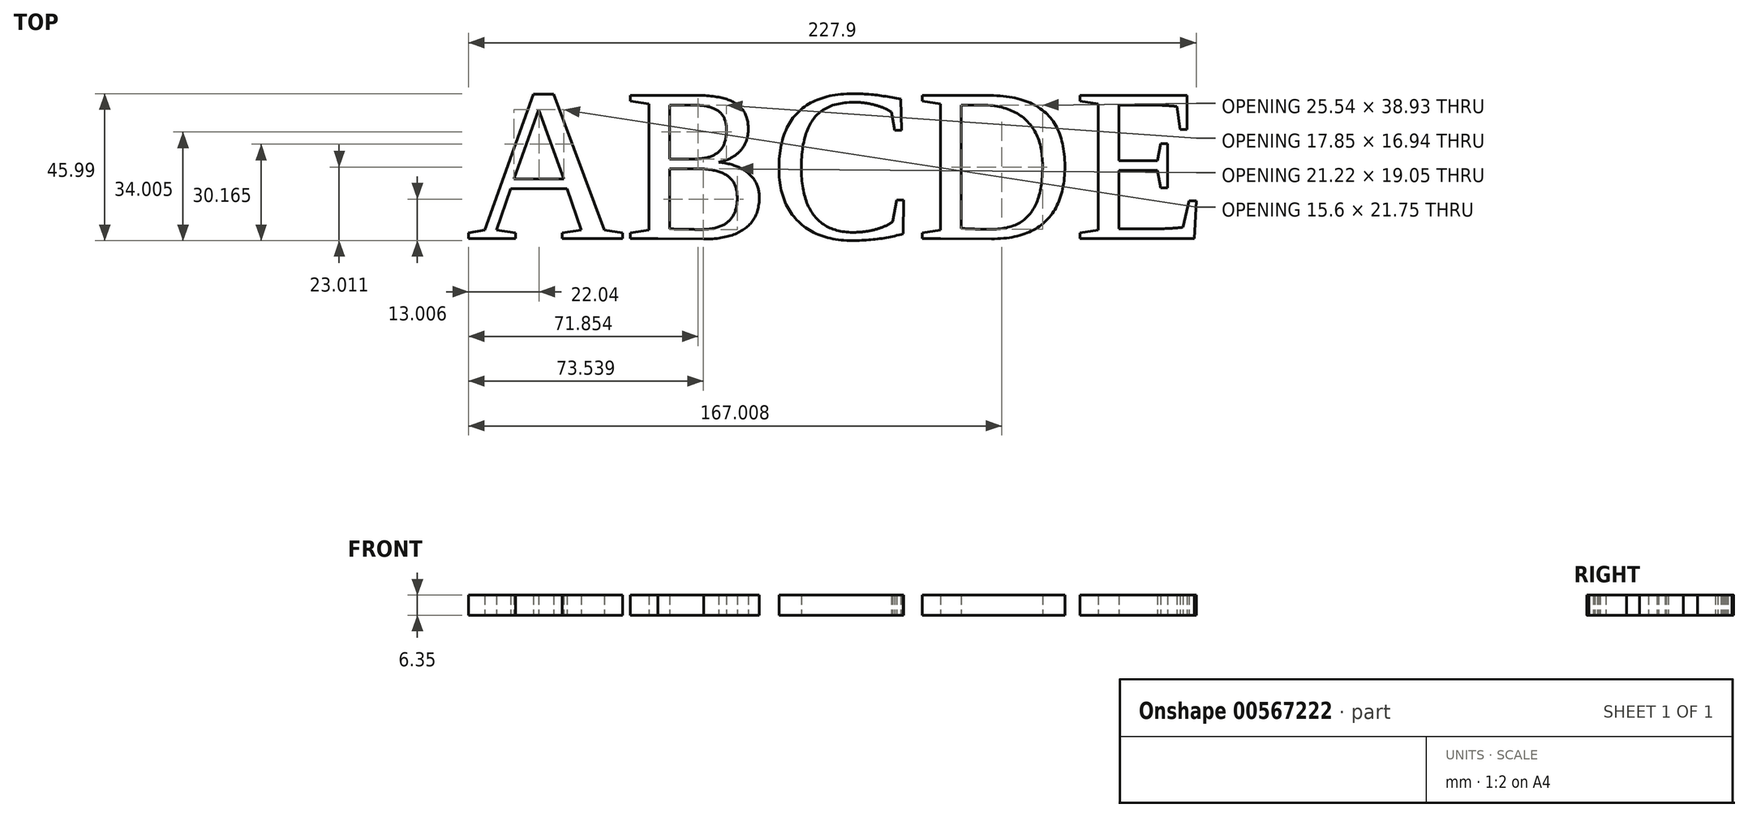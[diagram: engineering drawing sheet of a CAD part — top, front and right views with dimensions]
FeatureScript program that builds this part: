
annotation { "Feature Type Name" : "Feature", "Feature Type Description" : "" }
export const myFeature = defineFeature(function(context is Context, id is Id, definition is map)
    precondition{}
    {
        {
            var Q0;
            Q0=qCreatedBy(makeId("Top.planeOp"),FACE);
            var sketch = newSketch(context, id + "F0", { "sketchPlane" : qUnion([Q0])});
            skText(sketch, "E0", { "text": "ABCDE", "fontName": "Tinos-Regular.ttf"});
            const initialGuessF0  = {"E0": [0, 0, 1, 0, 0.04928]};
            skSetInitialGuess(sketch, initialGuessF0);
            skSolve(sketch);
        }
        {
            var Q0;
            Q0=makeQuery(id+"F0.imprint","IMPRINT",FACE,{"disambiguationData":[TD([[makeQuery(id+"F0.imprint","IMPRINT",EDGE,{"derivedFrom":sQuery(id+"F0.wireOp",EDGE,"E0.sketch_text.stroke-69")}),-1.0]])]});
            var Q1;
            Q1=makeQuery(id+"F0.imprint","IMPRINT",FACE,{"disambiguationData":[TD([[makeQuery(id+"F0.imprint","IMPRINT",EDGE,{"derivedFrom":sQuery(id+"F0.wireOp",EDGE,"E0.sketch_text.stroke-19")}),-1.0]])]});
            var Q2;
            Q2=makeQuery(id+"F0.imprint","IMPRINT",FACE,{"disambiguationData":[TD([[makeQuery(id+"F0.imprint","IMPRINT",EDGE,{"derivedFrom":sQuery(id+"F0.wireOp",EDGE,"E0.sketch_text.stroke-0")}),-1.0]])]});
            var Q3;
            Q3=makeQuery(id+"F0.imprint","IMPRINT",FACE,{"disambiguationData":[TD([[makeQuery(id+"F0.imprint","IMPRINT",EDGE,{"derivedFrom":sQuery(id+"F0.wireOp",EDGE,"E0.sketch_text.stroke-49")}),-1.0]])]});
            var Q4;
            Q4=makeQuery(id+"F0.imprint","IMPRINT",FACE,{"disambiguationData":[TD([[makeQuery(id+"F0.imprint","IMPRINT",EDGE,{"derivedFrom":sQuery(id+"F0.wireOp",EDGE,"E0.sketch_text.stroke-88")}),-1.0]])]});
            extrude(context, id + "F1", {"entities" : qUnion([Q0, Q1, Q2, Q3, Q4]), "depth" : 6.35 * mm, "offsetDistance" : 25.4 * mm});
        }
    });
